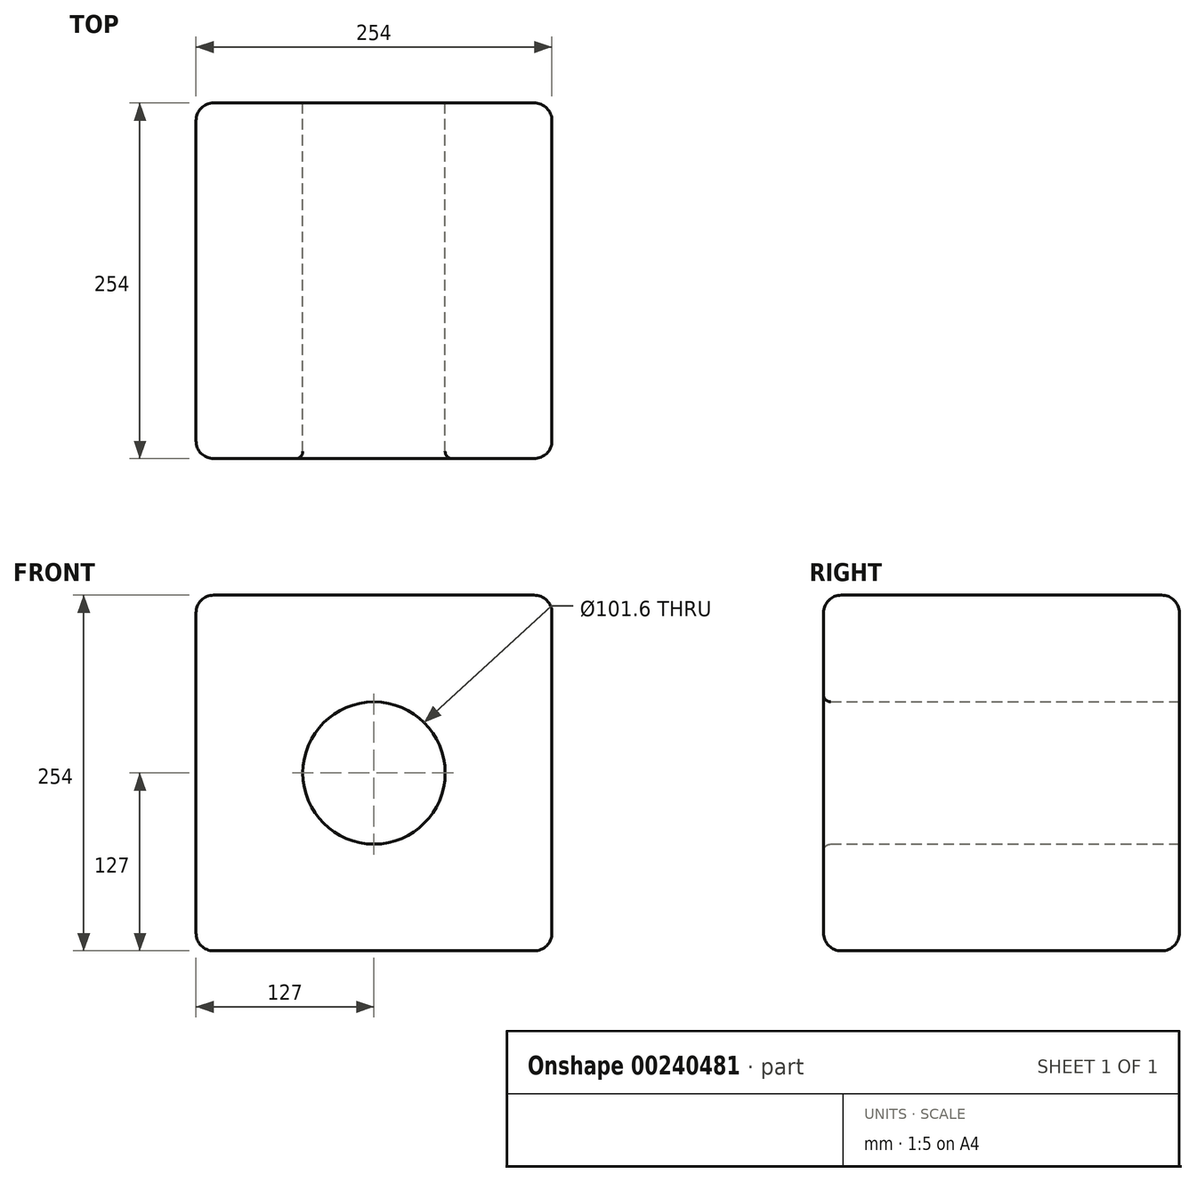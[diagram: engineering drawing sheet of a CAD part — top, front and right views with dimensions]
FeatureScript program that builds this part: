
annotation { "Feature Type Name" : "Feature", "Feature Type Description" : "" }
export const myFeature = defineFeature(function(context is Context, id is Id, definition is map)
    precondition{}
    {
        {
            var Q0;
            Q0=qCreatedBy(makeId("Front.planeOp"),FACE);
            var sketch = newSketch(context, id + "F0", { "sketchPlane" : qUnion([Q0])});
            skLineSegment(sketch, "E0.bottom", {"start": v(127, 127) * mm, "end": v(-127, 127) * mm});
            skLineSegment(sketch, "E0.top", {"start": v(127, -127) * mm, "end": v(-127, -127) * mm});
            skLineSegment(sketch, "E0.left", {"start": v(127, 127) * mm, "end": v(127, -127) * mm});
            skLineSegment(sketch, "E0.right", {"start": v(-127, 127) * mm, "end": v(-127, -127) * mm});
            skPoint(sketch, "E0.middle", {"position": v(0, 0) * mm});
            skSolve(sketch);
        }
        {
            var Q0;
            Q0 = qSketchRegion(id + "F0", true);
            extrude(context, id + "F1", {"entities" : qUnion([Q0]), "endBound" : BoundingType.SYMMETRIC, "depth" : 254 * mm});
        }
        {
            var Q0;
            Q0=makeQuery(id+"F1.opExtrude","CAP_FACE",FACE,{"disambiguationData":[OSD([sQuery(id+"F0.wireOp",EDGE,"E0.bottom"),sQuery(id+"F0.wireOp",EDGE,"E0.top"),sQuery(id+"F0.wireOp",EDGE,"E0.left"),sQuery(id+"F0.wireOp",EDGE,"E0.right")])],"isStart":false});
            var Q1;
            Q1=makeQuery(id+"F1.opExtrude","SWEPT_FACE",FACE,{"disambiguationData":[OSD([sQuery(id+"F0.wireOp",EDGE,"E0.right")])]});
            var Q2;
            Q2=makeQuery(id+"F1.opExtrude","SWEPT_FACE",FACE,{"disambiguationData":[OSD([sQuery(id+"F0.wireOp",EDGE,"E0.bottom")])]});
            var Q3;
            Q3=makeQuery(id+"F1.opExtrude","CAP_FACE",FACE,{"disambiguationData":[OSD([sQuery(id+"F0.wireOp",EDGE,"E0.bottom"),sQuery(id+"F0.wireOp",EDGE,"E0.top"),sQuery(id+"F0.wireOp",EDGE,"E0.left"),sQuery(id+"F0.wireOp",EDGE,"E0.right")])],"isStart":true});
            var Q4;
            Q4=makeQuery(id+"F1.opExtrude","CAP_EDGE",EDGE,{"disambiguationData":[OSD([sQuery(id+"F0.wireOp",EDGE,"E0.top")])],"isStart":false});
            var Q5;
            Q5=makeQuery(id+"F1.opExtrude","SWEPT_FACE",FACE,{"disambiguationData":[OSD([sQuery(id+"F0.wireOp",EDGE,"E0.top")])]});
            var Q6;
            Q6=makeQuery(id+"F1.opExtrude","SWEPT_FACE",FACE,{"disambiguationData":[OSD([sQuery(id+"F0.wireOp",EDGE,"E0.left")])]});
            fillet(context, id + "F2", {"entities" : qUnion([Q0, Q1, Q2, Q3, Q4, Q5, Q6]), "radius" : 12.7 * mm, "tangentPropagation" : true, "allowEdgeOverflow" : false});
        }
        {
            var Q0;
            Q0=makeQuery(id+"F1.opExtrude","CAP_FACE",FACE,{"disambiguationData":[OSD([sQuery(id+"F0.wireOp",EDGE,"E0.bottom"),sQuery(id+"F0.wireOp",EDGE,"E0.top"),sQuery(id+"F0.wireOp",EDGE,"E0.left"),sQuery(id+"F0.wireOp",EDGE,"E0.right")])],"isStart":true});
            var sketch = newSketch(context, id + "F3", { "sketchPlane" : qUnion([Q0])});
            skCircle(sketch, "E1", {"center": v(0, 0) * mm, "radius": 50.8 * mm});
            skSolve(sketch);
        }
        {
            var Q0;
            Q0=makeQuery(id+"F3.imprint","IMPRINT",FACE,{"disambiguationData":[TD([[makeQuery(id+"F3.imprint","IMPRINT",EDGE,{"derivedFrom":sQuery(id+"F3.wireOp",EDGE,"E1")}),1.0]])]});
            var Q1;
            Q1=sQuery(id+"F3.wireOp",EDGE,"E1");
            extrude(context, id + "F4", {"entities" : qUnion([Q0]), "operationType" : NewBodyOperationType.REMOVE, "surfaceEntities" : qUnion([Q1]), "endBound" : BoundingType.THROUGH_ALL, "oppositeDirection" : true, "depth" : 25.4 * mm});
        }
        {
            var Q0;
            Q0=makeQuery(id+"F4.boolean.opBoolean","COPY",EDGE,{"derivedFrom":makeQuery(id+"F4.opExtrude","CAP_EDGE",EDGE,{"disambiguationData":[OSD([sQuery(id+"F3.wireOp",EDGE,"E1")])],"isStart":true})});
            var Q1;
            Q1=makeQuery(id+"F4.boolean.opBoolean","INTERSECT",EDGE,{"derivedFrom":[makeQuery(id+"F1.opExtrude","CAP_FACE",FACE,{"disambiguationData":[OSD([sQuery(id+"F0.wireOp",EDGE,"E0.bottom"),sQuery(id+"F0.wireOp",EDGE,"E0.top"),sQuery(id+"F0.wireOp",EDGE,"E0.left"),sQuery(id+"F0.wireOp",EDGE,"E0.right")])],"isStart":false}),makeQuery(id+"F4.opExtrude","SWEPT_FACE",FACE,{"disambiguationData":[OSD([sQuery(id+"F3.wireOp",EDGE,"E1")])]})]});
            fillet(context, id + "F5", {"entities" : qUnion([Q0, Q1]), "radius" : 5.08 * mm, "tangentPropagation" : true, "allowEdgeOverflow" : false});
        }
    });
